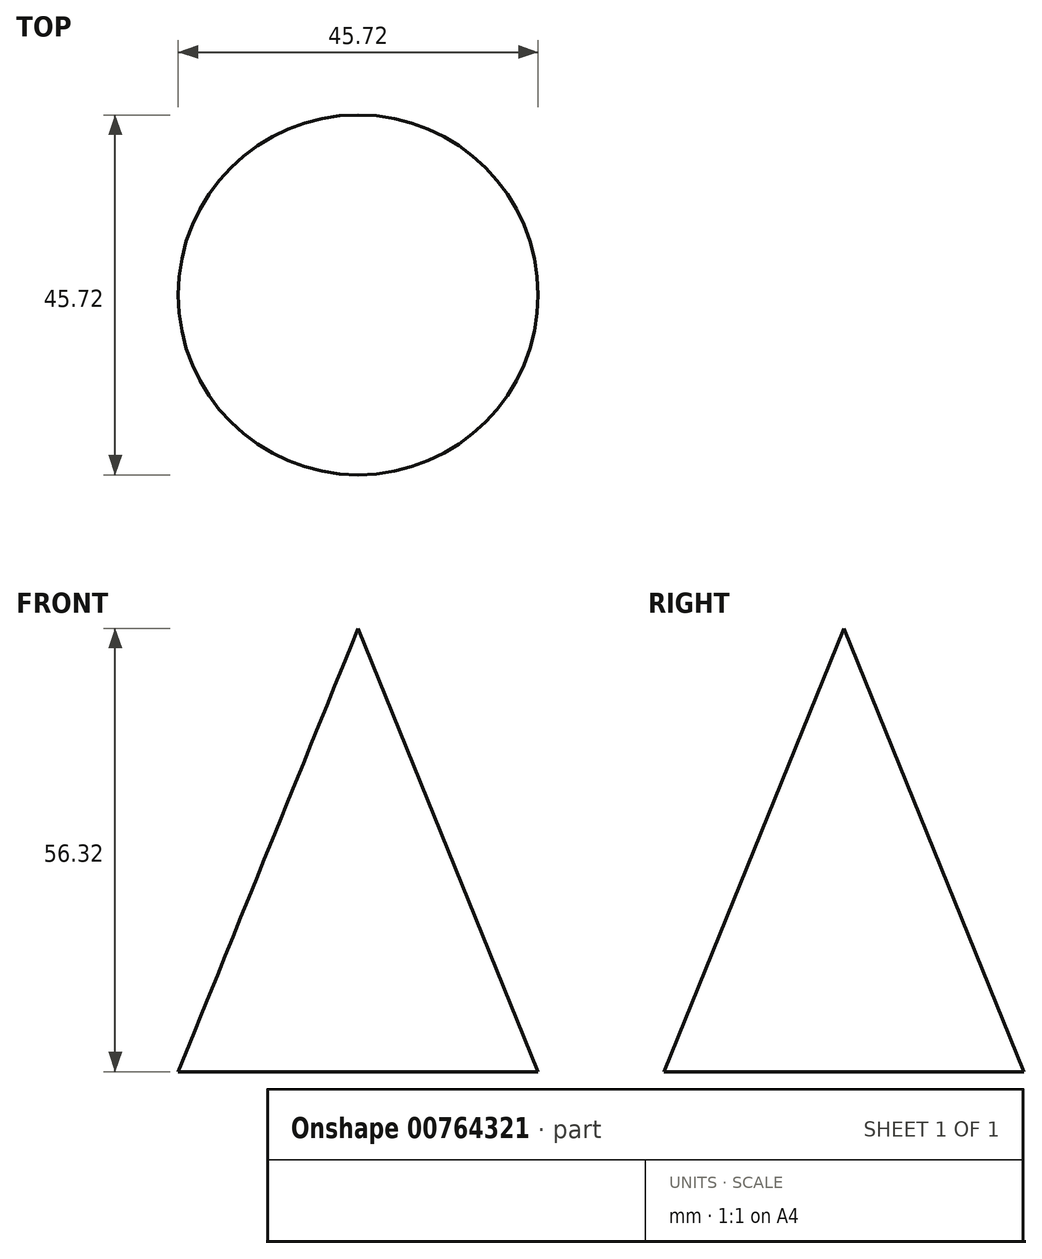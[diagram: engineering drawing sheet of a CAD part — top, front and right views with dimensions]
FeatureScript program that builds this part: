
annotation { "Feature Type Name" : "Feature", "Feature Type Description" : "" }
export const myFeature = defineFeature(function(context is Context, id is Id, definition is map)
    precondition{}
    {
        {
            var Q0;
            Q0=qCreatedBy(makeId("Front.planeOp"),FACE);
            var sketch = newSketch(context, id + "F0", { "sketchPlane" : qUnion([Q0])});
            skLineSegment(sketch, "E0", {"start": v(-36.41, 56.32) * mm, "end": v(-59.27, 0) * mm});
            skLineSegment(sketch, "E1", {"start": v(-36.41, 56.32) * mm, "end": v(-36.41, 0) * mm});
            skLineSegment(sketch, "E2", {"start": v(-36.41, 0) * mm, "end": v(-59.27, 0) * mm});
            skSolve(sketch);
        }
        {
            var Q0;
            Q0=makeQuery(id+"F0.imprint","IMPRINT",FACE,{"disambiguationData":[TD([[makeQuery(id+"F0.imprint","IMPRINT",EDGE,{"derivedFrom":sQuery(id+"F0.wireOp",EDGE,"E0")}),1.0]])]});
            var Q1;
            Q1=sQuery(id+"F0.wireOp",EDGE,"E1");
            revolve(context, id + "F1", {"surfaceOperationType" : NewSurfaceOperationType.NEW, "entities" : qUnion([Q0]), "axis" : qUnion([Q1]), "revolveType" : RevolveType.FULL});
        }
        {
            var Q0;
            Q0=qCreatedBy(makeId("Top.planeOp"),FACE);
            var sketch = newSketch(context, id + "F2", { "sketchPlane" : qUnion([Q0])});
            skLineSegment(sketch, "E3", {"start": v(-45.07, 27) * mm, "end": v(-45.07, -27.75) * mm});
            skSolve(sketch);
        }
        {
            var Q0;
            Q0=sQuery(id+"F2.wireOp",EDGE,"E3");
            extrude(context, id + "F3", {"bodyType" : ToolBodyType.SURFACE, "surfaceEntities" : qUnion([Q0]), "endBound" : BoundingType.SYMMETRIC, "depth" : 125.98 * mm, "offsetDistance" : 25.4 * mm});
        }
        {
            var Q0;
            Q0=qCreatedBy(makeId("Front.planeOp"),FACE);
            var sketch = newSketch(context, id + "F4", { "sketchPlane" : qUnion([Q0])});
            skLineSegment(sketch, "E4", {"start": v(-65.72, 40.47) * mm, "end": v(-4.52, 40.47) * mm});
            skSolve(sketch);
        }
        {
            var Q0;
            Q0=sQuery(id+"F4.wireOp",EDGE,"E4");
            extrude(context, id + "F5", {"bodyType" : ToolBodyType.SURFACE, "surfaceEntities" : qUnion([Q0]), "endBound" : BoundingType.SYMMETRIC, "depth" : 114.3 * mm, "offsetDistance" : 25.4 * mm});
        }
    });
